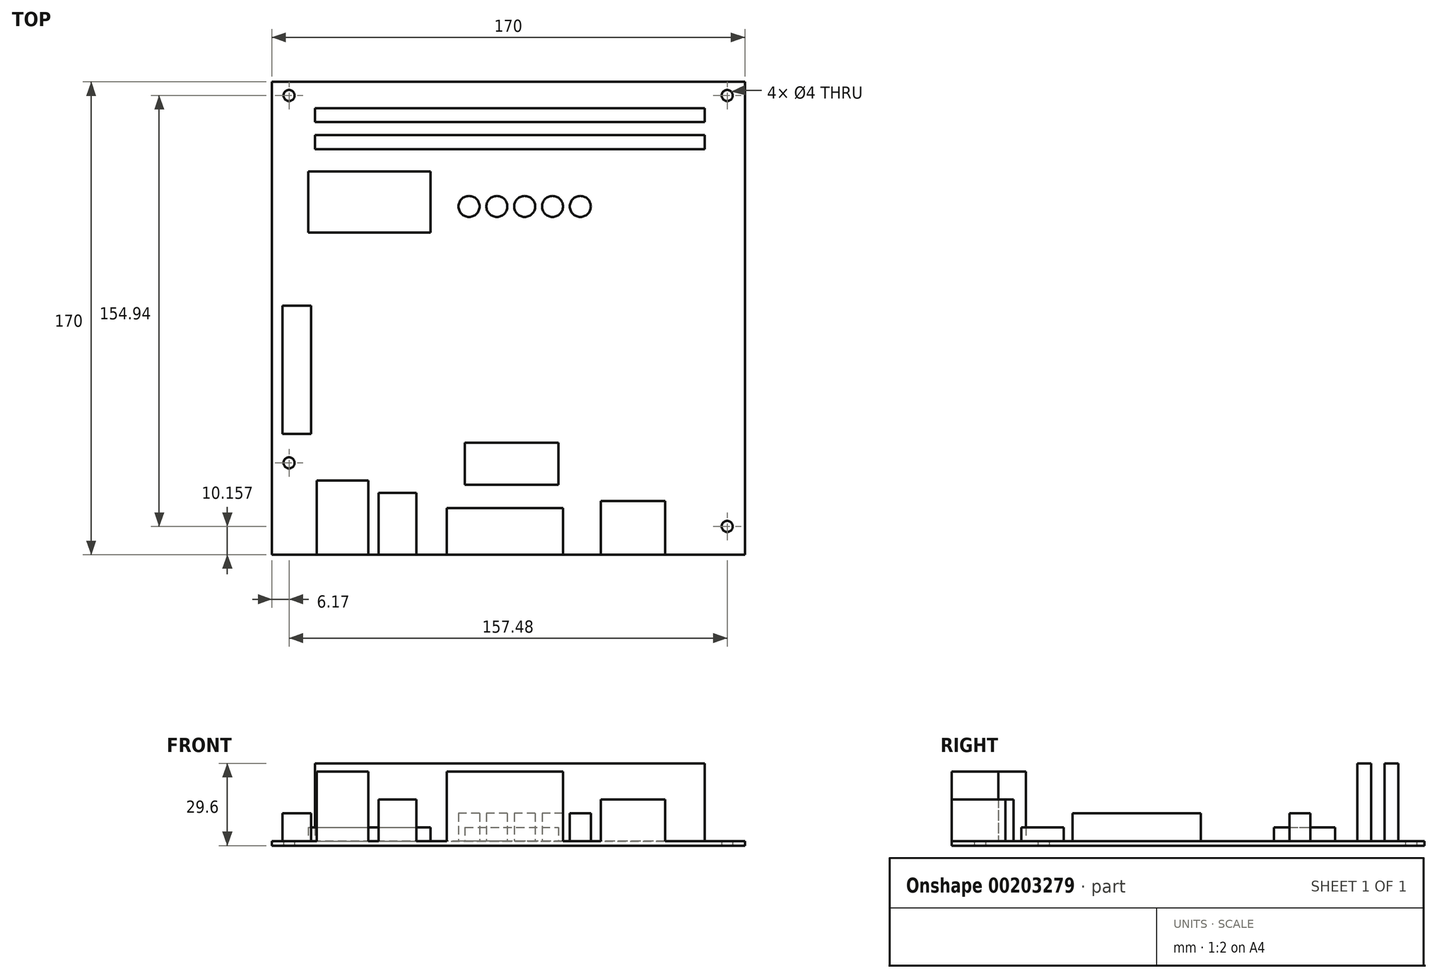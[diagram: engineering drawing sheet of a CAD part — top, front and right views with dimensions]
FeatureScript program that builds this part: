
annotation { "Feature Type Name" : "Feature", "Feature Type Description" : "" }
export const myFeature = defineFeature(function(context is Context, id is Id, definition is map)
    precondition{}
    {
        {
            var Q0;
            Q0=qCreatedBy(makeId("Top.planeOp"),FACE);
            var sketch = newSketch(context, id + "F0", { "sketchPlane" : qUnion([Q0])});
            skLineSegment(sketch, "E0.bottom", {"start": v(-40.76, 122.18) * mm, "end": v(129.24, 122.18) * mm});
            skLineSegment(sketch, "E0.top", {"start": v(-40.76, -47.82) * mm, "end": v(129.24, -47.82) * mm});
            skLineSegment(sketch, "E0.left", {"start": v(-40.76, 122.18) * mm, "end": v(-40.76, -47.82) * mm});
            skLineSegment(sketch, "E0.right", {"start": v(129.24, 122.18) * mm, "end": v(129.24, -47.82) * mm});
            skLineSegment(sketch, "E1", {"start": v(129.24, -47.82) * mm, "end": v(129.24, -37.66) * mm, "construction": true});
            skLineSegment(sketch, "E2", {"start": v(129.24, -37.66) * mm, "end": v(122.89, -37.66) * mm, "construction": true});
            skLineSegment(sketch, "E3", {"start": v(129.24, 122.18) * mm, "end": v(129.24, 117.28) * mm, "construction": true});
            skLineSegment(sketch, "E4", {"start": v(129.24, 117.28) * mm, "end": v(122.89, 117.28) * mm, "construction": true});
            skLineSegment(sketch, "E5", {"start": v(122.89, 117.28) * mm, "end": v(122.89, -37.66) * mm, "construction": true});
            skLineSegment(sketch, "E6", {"start": v(122.89, -37.66) * mm, "end": v(-34.6, -37.66) * mm, "construction": true});
            skLineSegment(sketch, "E7", {"start": v(-34.6, -14.8) * mm, "end": v(-34.6, -37.66) * mm, "construction": true});
            skLineSegment(sketch, "E8", {"start": v(-34.6, -14.8) * mm, "end": v(-34.6, 117.28) * mm, "construction": true});
            skCircle(sketch, "E9", {"center": v(-34.6, 117.28) * mm, "radius": 2 * mm});
            skCircle(sketch, "E10", {"center": v(122.89, 117.28) * mm, "radius": 2 * mm});
            skCircle(sketch, "E11", {"center": v(122.89, -37.66) * mm, "radius": 2 * mm});
            skCircle(sketch, "E12", {"center": v(-34.6, -14.8) * mm, "radius": 2 * mm});
            skSolve(sketch);
        }
        {
            var Q0;
            Q0=makeQuery(id+"F0.imprint","IMPRINT",FACE,{"disambiguationData":[TD([[makeQuery(id+"F0.imprint","IMPRINT",EDGE,{"derivedFrom":sQuery(id+"F0.wireOp",EDGE,"E0.bottom")}),-1.0]])]});
            extrude(context, id + "F1", {"entities" : qUnion([Q0]), "depth" : 1.6 * mm});
        }
        {
            var Q0;
            Q0=makeQuery(id+"F1.opExtrude","CAP_FACE",FACE,{"disambiguationData":[OSD([sQuery(id+"F0.wireOp",EDGE,"E0.bottom"),sQuery(id+"F0.wireOp",EDGE,"E0.top"),sQuery(id+"F0.wireOp",EDGE,"E0.left"),sQuery(id+"F0.wireOp",EDGE,"E0.right"),sQuery(id+"F0.wireOp",EDGE,"E9"),sQuery(id+"F0.wireOp",EDGE,"E10"),sQuery(id+"F0.wireOp",EDGE,"E11"),sQuery(id+"F0.wireOp",EDGE,"E12")])],"isStart":false});
            var sketch = newSketch(context, id + "F2", { "sketchPlane" : qUnion([Q0])});
            skLineSegment(sketch, "E13.bottom", {"start": v(114.78, 112.72) * mm, "end": v(-25.22, 112.72) * mm});
            skLineSegment(sketch, "E13.top", {"start": v(114.78, 107.72) * mm, "end": v(-25.22, 107.72) * mm});
            skLineSegment(sketch, "E13.left", {"start": v(114.78, 112.72) * mm, "end": v(114.78, 107.72) * mm});
            skLineSegment(sketch, "E13.right", {"start": v(-25.22, 112.72) * mm, "end": v(-25.22, 107.72) * mm});
            skLineSegment(sketch, "E14", {"start": v(114.78, 107.72) * mm, "end": v(114.78, 103) * mm, "construction": true});
            skLineSegment(sketch, "E15.bottom", {"start": v(114.78, 103) * mm, "end": v(-25.22, 103) * mm});
            skLineSegment(sketch, "E15.top", {"start": v(114.78, 98) * mm, "end": v(-25.22, 98) * mm});
            skLineSegment(sketch, "E15.left", {"start": v(114.78, 103) * mm, "end": v(114.78, 98) * mm});
            skLineSegment(sketch, "E15.right", {"start": v(-25.22, 103) * mm, "end": v(-25.22, 98) * mm});
            skLineSegment(sketch, "E16.bottom", {"start": v(-24.68, -47.82) * mm, "end": v(-6.12, -47.82) * mm});
            skLineSegment(sketch, "E16.top", {"start": v(-24.68, -21.1) * mm, "end": v(-6.12, -21.1) * mm});
            skLineSegment(sketch, "E16.left", {"start": v(-24.68, -47.82) * mm, "end": v(-24.68, -21.1) * mm});
            skLineSegment(sketch, "E16.right", {"start": v(-6.12, -47.82) * mm, "end": v(-6.12, -21.1) * mm});
            skLineSegment(sketch, "E17.bottom", {"start": v(11.2, -47.82) * mm, "end": v(-2.4, -47.82) * mm});
            skLineSegment(sketch, "E17.top", {"start": v(11.2, -25.56) * mm, "end": v(-2.4, -25.56) * mm});
            skLineSegment(sketch, "E17.left", {"start": v(11.2, -47.82) * mm, "end": v(11.2, -25.56) * mm});
            skLineSegment(sketch, "E17.right", {"start": v(-2.4, -47.82) * mm, "end": v(-2.4, -25.56) * mm});
            skLineSegment(sketch, "E18.bottom", {"start": v(22.1, -47.82) * mm, "end": v(63.91, -47.82) * mm});
            skLineSegment(sketch, "E18.top", {"start": v(22.1, -31) * mm, "end": v(63.91, -31) * mm});
            skLineSegment(sketch, "E18.left", {"start": v(22.1, -47.82) * mm, "end": v(22.1, -31) * mm});
            skLineSegment(sketch, "E18.right", {"start": v(63.91, -47.82) * mm, "end": v(63.91, -31) * mm});
            skLineSegment(sketch, "E19.bottom", {"start": v(100.54, -47.82) * mm, "end": v(77.52, -47.82) * mm});
            skLineSegment(sketch, "E19.top", {"start": v(100.54, -28.53) * mm, "end": v(77.52, -28.53) * mm});
            skLineSegment(sketch, "E19.left", {"start": v(100.54, -47.82) * mm, "end": v(100.54, -28.53) * mm});
            skLineSegment(sketch, "E19.right", {"start": v(77.52, -47.82) * mm, "end": v(77.52, -28.53) * mm});
            skCircle(sketch, "E20", {"center": v(70.1, 77.4) * mm, "radius": 3.77 * mm});
            skCircle(sketch, "E21.1.0.0", {"center": v(60.1, 77.4) * mm, "radius": 3.77 * mm});
            skCircle(sketch, "E21.2.0.0", {"center": v(50.1, 77.4) * mm, "radius": 3.77 * mm});
            skCircle(sketch, "E21.3.0.0", {"center": v(40.1, 77.4) * mm, "radius": 3.77 * mm});
            skCircle(sketch, "E21.4.0.0", {"center": v(30.1, 77.4) * mm, "radius": 3.77 * mm});
            skLineSegment(sketch, "E21.direction1", {"start": v(70.1, 77.4) * mm, "end": v(60.1, 77.4) * mm, "construction": true});
            skLineSegment(sketch, "E22.bottom", {"start": v(28.64, -22.73) * mm, "end": v(62.2, -22.73) * mm});
            skLineSegment(sketch, "E22.top", {"start": v(28.64, -7.53) * mm, "end": v(62.2, -7.53) * mm});
            skLineSegment(sketch, "E22.left", {"start": v(28.64, -22.73) * mm, "end": v(28.64, -7.53) * mm});
            skLineSegment(sketch, "E22.right", {"start": v(62.2, -22.73) * mm, "end": v(62.2, -7.53) * mm});
            skLineSegment(sketch, "E23.bottom", {"start": v(-36.9, -4.38) * mm, "end": v(-26.68, -4.38) * mm});
            skLineSegment(sketch, "E23.top", {"start": v(-36.9, 41.76) * mm, "end": v(-26.68, 41.76) * mm});
            skLineSegment(sketch, "E23.left", {"start": v(-36.9, -4.38) * mm, "end": v(-36.9, 41.76) * mm});
            skLineSegment(sketch, "E23.right", {"start": v(-26.68, -4.38) * mm, "end": v(-26.68, 41.76) * mm});
            skLineSegment(sketch, "E24.bottom", {"start": v(-27.73, 67.98) * mm, "end": v(16.32, 67.98) * mm});
            skLineSegment(sketch, "E24.top", {"start": v(-27.73, 90) * mm, "end": v(16.32, 90) * mm});
            skLineSegment(sketch, "E24.left", {"start": v(-27.73, 67.98) * mm, "end": v(-27.73, 90) * mm});
            skLineSegment(sketch, "E24.right", {"start": v(16.32, 67.98) * mm, "end": v(16.32, 90) * mm});
            skSolve(sketch);
        }
        {
            var Q0;
            Q0=makeQuery(id+"F2.imprint","IMPRINT",FACE,{"disambiguationData":[TD([[makeQuery(id+"F2.imprint","IMPRINT",EDGE,{"derivedFrom":sQuery(id+"F2.wireOp",EDGE,"E15.bottom")}),1.0]])]});
            var Q1;
            Q1=makeQuery(id+"F2.imprint","IMPRINT",FACE,{"disambiguationData":[TD([[makeQuery(id+"F2.imprint","IMPRINT",EDGE,{"derivedFrom":sQuery(id+"F2.wireOp",EDGE,"E13.bottom")}),1.0]])]});
            extrude(context, id + "F3", {"entities" : qUnion([Q0, Q1]), "operationType" : NewBodyOperationType.ADD, "depth" : 28 * mm});
        }
        {
            var Q0;
            Q0=makeQuery(id+"F2.imprint","IMPRINT",FACE,{"disambiguationData":[TD([[makeQuery(id+"F2.imprint","IMPRINT",EDGE,{"derivedFrom":sQuery(id+"F2.wireOp",EDGE,"E16.bottom")}),1.0]])]});
            var Q1;
            Q1=makeQuery(id+"F2.imprint","IMPRINT",FACE,{"disambiguationData":[TD([[makeQuery(id+"F2.imprint","IMPRINT",EDGE,{"derivedFrom":sQuery(id+"F2.wireOp",EDGE,"E18.bottom")}),1.0]])]});
            extrude(context, id + "F4", {"entities" : qUnion([Q0, Q1]), "operationType" : NewBodyOperationType.ADD, "depth" : 25 * mm});
        }
        {
            var Q0;
            Q0=makeQuery(id+"F2.imprint","IMPRINT",FACE,{"disambiguationData":[TD([[makeQuery(id+"F2.imprint","IMPRINT",EDGE,{"derivedFrom":sQuery(id+"F2.wireOp",EDGE,"E17.bottom")}),1.0]])]});
            var Q1;
            Q1=makeQuery(id+"F2.imprint","IMPRINT",FACE,{"disambiguationData":[TD([[makeQuery(id+"F2.imprint","IMPRINT",EDGE,{"derivedFrom":sQuery(id+"F2.wireOp",EDGE,"E19.bottom")}),1.0]])]});
            extrude(context, id + "F5", {"entities" : qUnion([Q0, Q1]), "operationType" : NewBodyOperationType.ADD, "depth" : 15 * mm});
        }
        {
            var Q0;
            Q0=makeQuery(id+"F2.imprint","IMPRINT",FACE,{"disambiguationData":[TD([[makeQuery(id+"F2.imprint","IMPRINT",EDGE,{"derivedFrom":sQuery(id+"F2.wireOp",EDGE,"E21.4.0.0")}),1.0]])]});
            var Q1;
            Q1=makeQuery(id+"F2.imprint","IMPRINT",FACE,{"disambiguationData":[TD([[makeQuery(id+"F2.imprint","IMPRINT",EDGE,{"derivedFrom":sQuery(id+"F2.wireOp",EDGE,"E21.3.0.0")}),1.0]])]});
            var Q2;
            Q2=makeQuery(id+"F2.imprint","IMPRINT",FACE,{"disambiguationData":[TD([[makeQuery(id+"F2.imprint","IMPRINT",EDGE,{"derivedFrom":sQuery(id+"F2.wireOp",EDGE,"E21.2.0.0")}),1.0]])]});
            var Q3;
            Q3=makeQuery(id+"F2.imprint","IMPRINT",FACE,{"disambiguationData":[TD([[makeQuery(id+"F2.imprint","IMPRINT",EDGE,{"derivedFrom":sQuery(id+"F2.wireOp",EDGE,"E21.1.0.0")}),1.0]])]});
            var Q4;
            Q4=makeQuery(id+"F2.imprint","IMPRINT",FACE,{"disambiguationData":[TD([[makeQuery(id+"F2.imprint","IMPRINT",EDGE,{"derivedFrom":sQuery(id+"F2.wireOp",EDGE,"E20")}),1.0]])]});
            extrude(context, id + "F6", {"entities" : qUnion([Q0, Q1, Q2, Q3, Q4]), "operationType" : NewBodyOperationType.ADD, "depth" : 10 * mm});
        }
        {
            var Q0;
            Q0=makeQuery(id+"F2.imprint","IMPRINT",FACE,{"disambiguationData":[TD([[makeQuery(id+"F2.imprint","IMPRINT",EDGE,{"derivedFrom":sQuery(id+"F2.wireOp",EDGE,"E22.bottom")}),1.0]])]});
            var Q1;
            Q1=makeQuery(id+"F2.imprint","IMPRINT",FACE,{"disambiguationData":[TD([[makeQuery(id+"F2.imprint","IMPRINT",EDGE,{"derivedFrom":sQuery(id+"F2.wireOp",EDGE,"E24.bottom")}),1.0]])]});
            extrude(context, id + "F7", {"entities" : qUnion([Q0, Q1]), "operationType" : NewBodyOperationType.ADD, "depth" : 5 * mm});
        }
        {
            var Q0;
            Q0=makeQuery(id+"F2.imprint","IMPRINT",FACE,{"disambiguationData":[TD([[makeQuery(id+"F2.imprint","IMPRINT",EDGE,{"derivedFrom":sQuery(id+"F2.wireOp",EDGE,"E23.bottom")}),1.0]])]});
            extrude(context, id + "F8", {"entities" : qUnion([Q0]), "operationType" : NewBodyOperationType.ADD, "depth" : 10 * mm});
        }
    });
